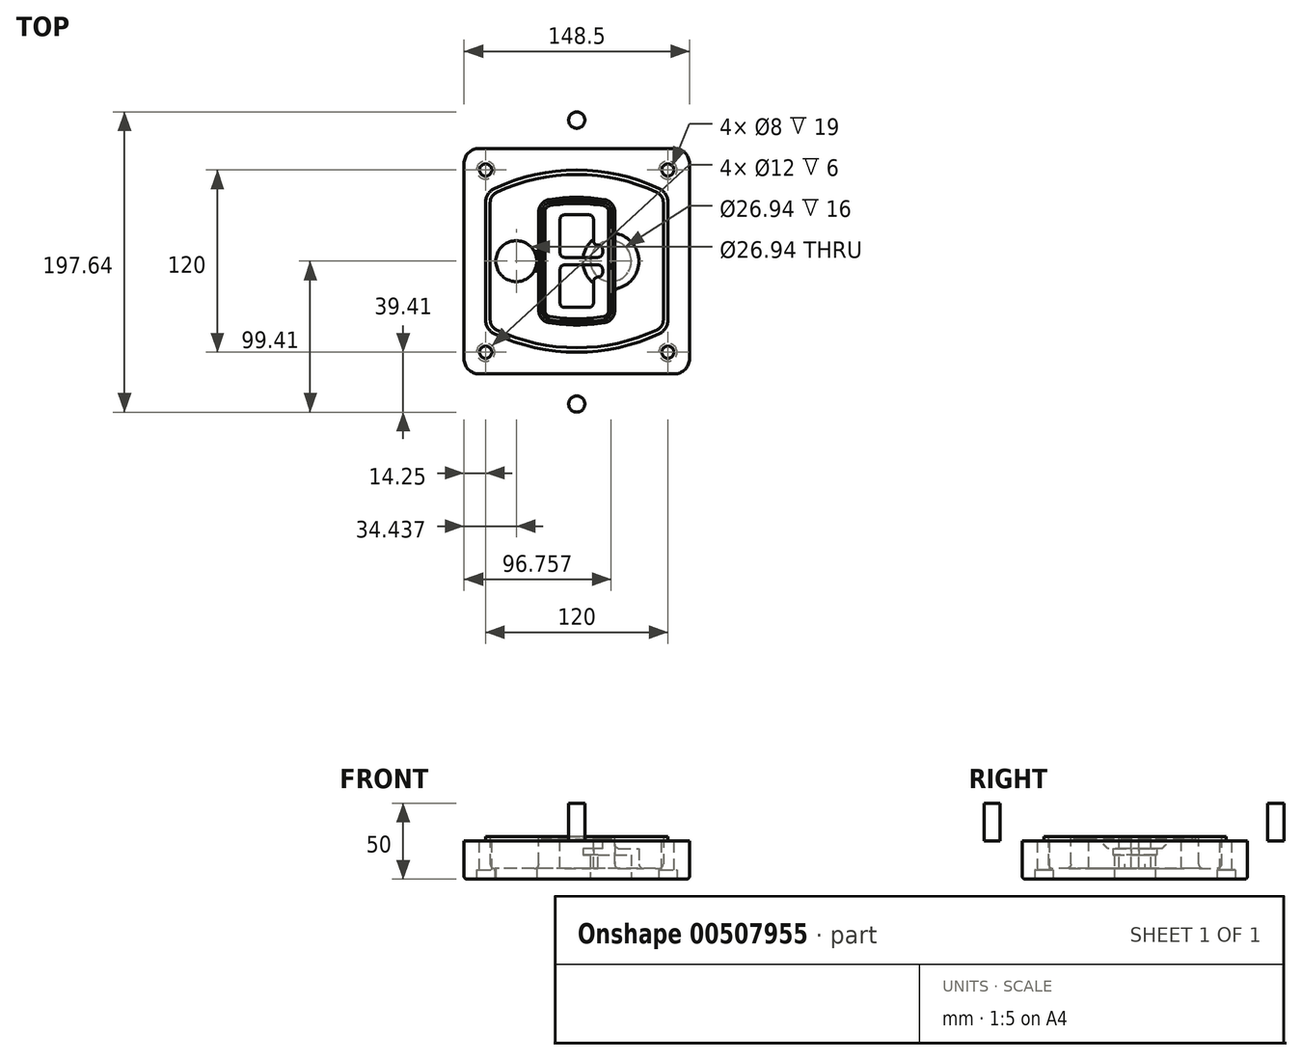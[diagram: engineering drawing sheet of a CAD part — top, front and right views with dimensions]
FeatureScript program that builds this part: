
annotation { "Feature Type Name" : "Feature", "Feature Type Description" : "" }
export const myFeature = defineFeature(function(context is Context, id is Id, definition is map)
    precondition{}
    {
        {
            var Q0;
            Q0=qCreatedBy(makeId("Top.planeOp"),FACE);
            var sketch = newSketch(context, id + "F0", { "sketchPlane" : qUnion([Q0])});
            skPoint(sketch, "E0.rect.middle", {"position": v(0, 0) * mm});
            skLineSegment(sketch, "E1.bottom", {"start": v(-64.25, -74.25) * mm, "end": v(64.25, -74.25) * mm});
            skLineSegment(sketch, "E1.top", {"start": v(-64.25, 74.25) * mm, "end": v(64.25, 74.25) * mm});
            skLineSegment(sketch, "E1.left", {"start": v(-74.25, -64.25) * mm, "end": v(-74.25, 64.25) * mm});
            skLineSegment(sketch, "E1.right", {"start": v(74.25, -64.25) * mm, "end": v(74.25, 64.25) * mm});
            skLineSegment(sketch, "E2", {"start": v(-74.25, 74.25) * mm, "end": v(74.25, -74.25) * mm, "construction": true});
            skLineSegment(sketch, "E3", {"start": v(74.25, 74.25) * mm, "end": v(-74.25, -74.25) * mm, "construction": true});
            skCircle(sketch, "E4", {"center": v(-60, 60) * mm, "radius": 4 * mm});
            skCircle(sketch, "E5", {"center": v(60, 60) * mm, "radius": 4 * mm});
            skCircle(sketch, "E6", {"center": v(60, -60) * mm, "radius": 4 * mm});
            skCircle(sketch, "E7", {"center": v(-60, -60) * mm, "radius": 4 * mm});
            skLineSegment(sketch, "E8", {"start": v(-60, 60) * mm, "end": v(60, 60) * mm, "construction": true});
            skLineSegment(sketch, "E9", {"start": v(60, 60) * mm, "end": v(60, -60) * mm, "construction": true});
            skLineSegment(sketch, "E10", {"start": v(60, -60) * mm, "end": v(-60, -60) * mm, "construction": true});
            skLineSegment(sketch, "E11", {"start": v(-60, -60) * mm, "end": v(-60, 60) * mm, "construction": true});
            skLineSegment(sketch, "E12", {"start": v(-60, 38.83) * mm, "end": v(-60, -38.83) * mm});
            skLineSegment(sketch, "E13", {"start": v(60, 38.83) * mm, "end": v(60, -38.83) * mm});
            skArc(sketch, "E14", {"start": v(54.26, 47.88) * mm, "mid": v(0, 60) * mm, "end": v(-54.26, 47.88) * mm});
            skArc(sketch, "E15", {"start": v(-54.26, -47.88) * mm, "mid": v(0, -60) * mm, "end": v(54.26, -47.88) * mm});
            skLineSegment(sketch, "E16", {"start": v(-60, 0) * mm, "end": v(60, 0) * mm, "construction": true});
            skPoint(sketch, "E17.visualSharp", {"position": v(-60, -45) * mm});
            skArc(sketch, "E17.filletArc", {"start": v(-60, -38.83) * mm, "mid": v(-58.44, -44.2) * mm, "end": v(-54.26, -47.88) * mm});
            skPoint(sketch, "E18.visualSharp", {"position": v(-60, 45) * mm});
            skArc(sketch, "E18.filletArc", {"start": v(-54.26, 47.88) * mm, "mid": v(-58.44, 44.2) * mm, "end": v(-60, 38.83) * mm});
            skPoint(sketch, "E19.visualSharp", {"position": v(60, 45) * mm});
            skArc(sketch, "E19.filletArc", {"start": v(60, 38.83) * mm, "mid": v(58.44, 44.2) * mm, "end": v(54.26, 47.88) * mm});
            skPoint(sketch, "E20.visualSharp", {"position": v(60, -45) * mm});
            skArc(sketch, "E20.filletArc", {"start": v(54.26, -47.88) * mm, "mid": v(58.44, -44.2) * mm, "end": v(60, -38.83) * mm});
            skPoint(sketch, "E21.visualSharp", {"position": v(-74.25, 74.25) * mm});
            skArc(sketch, "E21.filletArc", {"start": v(-64.25, 74.25) * mm, "mid": v(-71.32, 71.32) * mm, "end": v(-74.25, 64.25) * mm});
            skPoint(sketch, "E22.visualSharp", {"position": v(74.25, 74.25) * mm});
            skArc(sketch, "E22.filletArc", {"start": v(74.25, 64.25) * mm, "mid": v(71.32, 71.32) * mm, "end": v(64.25, 74.25) * mm});
            skPoint(sketch, "E23.visualSharp", {"position": v(74.25, -74.25) * mm});
            skArc(sketch, "E23.filletArc", {"start": v(64.25, -74.25) * mm, "mid": v(71.32, -71.32) * mm, "end": v(74.25, -64.25) * mm});
            skPoint(sketch, "E24.visualSharp", {"position": v(-74.25, -74.25) * mm});
            skArc(sketch, "E24.filletArc", {"start": v(-74.25, -64.25) * mm, "mid": v(-71.32, -71.32) * mm, "end": v(-64.25, -74.25) * mm});
            skArc(sketch, "E25.0", {"start": v(57, 38.83) * mm, "mid": v(55.9, 42.58) * mm, "end": v(52.98, 45.17) * mm});
            skLineSegment(sketch, "E25.1", {"start": v(57, 38.83) * mm, "end": v(57, -38.83) * mm});
            skArc(sketch, "E25.2", {"start": v(52.98, -45.17) * mm, "mid": v(55.9, -42.58) * mm, "end": v(57, -38.83) * mm});
            skArc(sketch, "E25.3", {"start": v(-52.98, -45.17) * mm, "mid": v(0, -57) * mm, "end": v(52.98, -45.17) * mm});
            skArc(sketch, "E25.4", {"start": v(-57, -38.83) * mm, "mid": v(-55.9, -42.58) * mm, "end": v(-52.98, -45.17) * mm});
            skArc(sketch, "E25.5", {"start": v(52.98, 45.17) * mm, "mid": v(0, 57) * mm, "end": v(-52.98, 45.17) * mm});
            skLineSegment(sketch, "E25.6", {"start": v(-57, 38.83) * mm, "end": v(-57, -38.83) * mm});
            skArc(sketch, "E25.7", {"start": v(-52.98, 45.17) * mm, "mid": v(-55.9, 42.58) * mm, "end": v(-57, 38.83) * mm});
            skArc(sketch, "E26.0", {"start": v(-55.96, 51.5) * mm, "mid": v(-61.82, 46.33) * mm, "end": v(-64, 38.83) * mm});
            skArc(sketch, "E26.1", {"start": v(55.96, 51.5) * mm, "mid": v(0, 64) * mm, "end": v(-55.96, 51.5) * mm});
            skArc(sketch, "E26.2", {"start": v(64, 38.83) * mm, "mid": v(61.82, 46.33) * mm, "end": v(55.96, 51.5) * mm});
            skLineSegment(sketch, "E26.3", {"start": v(64, 38.83) * mm, "end": v(64, -38.83) * mm});
            skArc(sketch, "E26.4", {"start": v(55.96, -51.5) * mm, "mid": v(61.82, -46.33) * mm, "end": v(64, -38.83) * mm});
            skLineSegment(sketch, "E26.5", {"start": v(-64, 38.83) * mm, "end": v(-64, -38.83) * mm});
            skArc(sketch, "E26.6", {"start": v(-55.96, -51.5) * mm, "mid": v(0, -64) * mm, "end": v(55.96, -51.5) * mm});
            skArc(sketch, "E26.7", {"start": v(-64, -38.83) * mm, "mid": v(-61.82, -46.33) * mm, "end": v(-55.96, -51.5) * mm});
            skSolve(sketch);
        }
        {
            var Q0;
            Q0=makeQuery(id+"F0.imprint","IMPRINT",FACE,{"disambiguationData":[TD([[makeQuery(id+"F0.imprint","IMPRINT",EDGE,{"derivedFrom":sQuery(id+"F0.wireOp",EDGE,"E1.bottom")}),1.0]])]});
            var Q1;
            Q1=makeQuery(id+"F0.imprint","IMPRINT",FACE,{"disambiguationData":[TD([[makeQuery(id+"F0.imprint","IMPRINT",EDGE,{"derivedFrom":sQuery(id+"F0.wireOp",EDGE,"E12")}),1.0]])]});
            var Q2;
            Q2=makeQuery(id+"F0.imprint","IMPRINT",FACE,{"disambiguationData":[TD([[makeQuery(id+"F0.imprint","IMPRINT",EDGE,{"derivedFrom":sQuery(id+"F0.wireOp",EDGE,"E25.0")}),1.0]])]});
            var Q3;
            Q3=makeQuery(id+"F0.imprint","IMPRINT",FACE,{"disambiguationData":[TD([[makeQuery(id+"F0.imprint","IMPRINT",EDGE,{"derivedFrom":sQuery(id+"F0.wireOp",EDGE,"E12")}),-1.0]])]});
            extrude(context, id + "F1", {"entities" : qUnion([Q0, Q1, Q2, Q3]), "oppositeDirection" : true, "depth" : 25 * mm});
        }
        {
            var Q0;
            Q0=makeQuery(id+"F0.imprint","IMPRINT",FACE,{"disambiguationData":[TD([[makeQuery(id+"F0.imprint","IMPRINT",EDGE,{"derivedFrom":sQuery(id+"F0.wireOp",EDGE,"E12")}),1.0]])]});
            extrude(context, id + "F2", {"entities" : qUnion([Q0]), "operationType" : NewBodyOperationType.ADD, "depth" : 3 * mm});
        }
        {
            var Q0;
            Q0=makeQuery(id+"F0.imprint","IMPRINT",FACE,{"disambiguationData":[TD([[makeQuery(id+"F0.imprint","IMPRINT",EDGE,{"derivedFrom":sQuery(id+"F0.wireOp",EDGE,"E25.0")}),1.0]])]});
            extrude(context, id + "F3", {"entities" : qUnion([Q0]), "operationType" : NewBodyOperationType.REMOVE, "oppositeDirection" : true, "depth" : 18 * mm});
        }
        {
            var Q0;
            Q0=makeQuery(id+"F2.opExtrude","CAP_FACE",FACE,{"disambiguationData":[OSD([sQuery(id+"F0.wireOp",EDGE,"E12"),sQuery(id+"F0.wireOp",EDGE,"E13"),sQuery(id+"F0.wireOp",EDGE,"E14"),sQuery(id+"F0.wireOp",EDGE,"E15"),sQuery(id+"F0.wireOp",EDGE,"E17.filletArc"),sQuery(id+"F0.wireOp",EDGE,"E18.filletArc"),sQuery(id+"F0.wireOp",EDGE,"E19.filletArc"),sQuery(id+"F0.wireOp",EDGE,"E20.filletArc"),sQuery(id+"F0.wireOp",EDGE,"E25.0"),sQuery(id+"F0.wireOp",EDGE,"E25.1"),sQuery(id+"F0.wireOp",EDGE,"E25.2"),sQuery(id+"F0.wireOp",EDGE,"E25.3"),sQuery(id+"F0.wireOp",EDGE,"E25.4"),sQuery(id+"F0.wireOp",EDGE,"E25.5"),sQuery(id+"F0.wireOp",EDGE,"E25.6"),sQuery(id+"F0.wireOp",EDGE,"E25.7")])],"isStart":false});
            var sketch = newSketch(context, id + "F4", { "sketchPlane" : qUnion([Q0])});
            skArc(sketch, "E27.0", {"start": v(-18.34, -40.45) * mm, "mid": v(0, -42) * mm, "end": v(18.34, -40.45) * mm});
            skArc(sketch, "E28.0", {"start": v(18.34, 40.45) * mm, "mid": v(0, 42) * mm, "end": v(-18.34, 40.45) * mm});
            skLineSegment(sketch, "E29", {"start": v(-25, 32.57) * mm, "end": v(-25, -32.57) * mm});
            skLineSegment(sketch, "E30", {"start": v(25, 32.57) * mm, "end": v(25, -32.57) * mm});
            skLineSegment(sketch, "E31", {"start": v(-25, 39.1) * mm, "end": v(25, 39.1) * mm, "construction": true});
            skLineSegment(sketch, "E32", {"start": v(-25, -39.1) * mm, "end": v(25, -39.1) * mm, "construction": true});
            skPoint(sketch, "E33.visualSharp", {"position": v(-25, 39.1) * mm});
            skArc(sketch, "E33.filletArc", {"start": v(-18.34, 40.45) * mm, "mid": v(-23.11, 37.73) * mm, "end": v(-25, 32.57) * mm});
            skPoint(sketch, "E34.visualSharp", {"position": v(25, 39.1) * mm});
            skArc(sketch, "E34.filletArc", {"start": v(25, 32.57) * mm, "mid": v(23.11, 37.73) * mm, "end": v(18.34, 40.45) * mm});
            skPoint(sketch, "E35.visualSharp", {"position": v(25, -39.1) * mm});
            skArc(sketch, "E35.filletArc", {"start": v(18.34, -40.45) * mm, "mid": v(23.11, -37.73) * mm, "end": v(25, -32.57) * mm});
            skPoint(sketch, "E36.visualSharp", {"position": v(-25, -39.1) * mm});
            skArc(sketch, "E36.filletArc", {"start": v(-25, -32.57) * mm, "mid": v(-23.11, -37.73) * mm, "end": v(-18.34, -40.45) * mm});
            skArc(sketch, "E37.0", {"start": v(52.98, 45.17) * mm, "mid": v(0, 57) * mm, "end": v(-52.98, 45.17) * mm});
            skArc(sketch, "E37.1", {"start": v(-52.98, 45.17) * mm, "mid": v(-55.9, 42.58) * mm, "end": v(-57, 38.83) * mm});
            skLineSegment(sketch, "E37.2", {"start": v(-57, 38.83) * mm, "end": v(-57, -38.83) * mm});
            skArc(sketch, "E37.3", {"start": v(-57, -38.83) * mm, "mid": v(-55.9, -42.58) * mm, "end": v(-52.98, -45.17) * mm});
            skArc(sketch, "E37.4", {"start": v(-52.98, -45.17) * mm, "mid": v(0, -57) * mm, "end": v(52.98, -45.17) * mm});
            skArc(sketch, "E37.5", {"start": v(52.98, -45.17) * mm, "mid": v(55.9, -42.58) * mm, "end": v(57, -38.83) * mm});
            skLineSegment(sketch, "E37.6", {"start": v(57, 38.83) * mm, "end": v(57, -38.83) * mm});
            skArc(sketch, "E37.7", {"start": v(57, 38.83) * mm, "mid": v(55.9, 42.58) * mm, "end": v(52.98, 45.17) * mm});
            skLineSegment(sketch, "E38.0", {"start": v(23, 32.57) * mm, "end": v(23, -32.57) * mm});
            skArc(sketch, "E38.1", {"start": v(18, -38.48) * mm, "mid": v(21.58, -36.44) * mm, "end": v(23, -32.57) * mm});
            skArc(sketch, "E38.2", {"start": v(-18, -38.48) * mm, "mid": v(0, -40) * mm, "end": v(18, -38.48) * mm});
            skArc(sketch, "E38.3", {"start": v(-23, -32.57) * mm, "mid": v(-21.58, -36.44) * mm, "end": v(-18, -38.48) * mm});
            skLineSegment(sketch, "E38.4", {"start": v(-23, 32.57) * mm, "end": v(-23, -32.57) * mm});
            skArc(sketch, "E38.5", {"start": v(23, 32.57) * mm, "mid": v(21.58, 36.44) * mm, "end": v(18, 38.48) * mm});
            skArc(sketch, "E38.6", {"start": v(-18, 38.48) * mm, "mid": v(-21.58, 36.44) * mm, "end": v(-23, 32.57) * mm});
            skArc(sketch, "E38.7", {"start": v(18, 38.48) * mm, "mid": v(0, 40) * mm, "end": v(-18, 38.48) * mm});
            skArc(sketch, "E39.0", {"start": v(21, 32.57) * mm, "mid": v(20.06, 35.15) * mm, "end": v(17.67, 36.5) * mm});
            skLineSegment(sketch, "E39.1", {"start": v(21, 32.57) * mm, "end": v(21, -32.57) * mm});
            skArc(sketch, "E39.2", {"start": v(17.67, -36.5) * mm, "mid": v(20.06, -35.15) * mm, "end": v(21, -32.57) * mm});
            skArc(sketch, "E39.3", {"start": v(-17.67, -36.5) * mm, "mid": v(0, -38) * mm, "end": v(17.67, -36.5) * mm});
            skArc(sketch, "E39.4", {"start": v(-21, -32.57) * mm, "mid": v(-20.06, -35.15) * mm, "end": v(-17.67, -36.5) * mm});
            skArc(sketch, "E39.5", {"start": v(17.67, 36.5) * mm, "mid": v(0, 38) * mm, "end": v(-17.67, 36.5) * mm});
            skLineSegment(sketch, "E39.6", {"start": v(-21, 32.57) * mm, "end": v(-21, -32.57) * mm});
            skArc(sketch, "E39.7", {"start": v(-17.67, 36.5) * mm, "mid": v(-20.06, 35.15) * mm, "end": v(-21, 32.57) * mm});
            skLineSegment(sketch, "E40", {"start": v(-25, 0) * mm, "end": v(25, 0) * mm, "construction": true});
            skLineSegment(sketch, "E41", {"start": v(-11, 5.5) * mm, "end": v(-11, 27.5) * mm});
            skLineSegment(sketch, "E42", {"start": v(-8, 30.5) * mm, "end": v(8, 30.5) * mm});
            skLineSegment(sketch, "E43", {"start": v(11, 27.5) * mm, "end": v(11, 13.5) * mm});
            skLineSegment(sketch, "E44", {"start": v(14, 10.5) * mm, "end": v(14, 10.5) * mm});
            skLineSegment(sketch, "E45", {"start": v(17, 7.5) * mm, "end": v(17, 5.5) * mm});
            skLineSegment(sketch, "E46", {"start": v(14, 2.5) * mm, "end": v(-8, 2.5) * mm});
            skPoint(sketch, "E47.visualSharp", {"position": v(-11, 30.5) * mm});
            skArc(sketch, "E47.filletArc", {"start": v(-8, 30.5) * mm, "mid": v(-10.12, 29.62) * mm, "end": v(-11, 27.5) * mm});
            skPoint(sketch, "E48.visualSharp", {"position": v(11, 30.5) * mm});
            skArc(sketch, "E48.filletArc", {"start": v(11, 27.5) * mm, "mid": v(10.12, 29.62) * mm, "end": v(8, 30.5) * mm});
            skPoint(sketch, "E49.visualSharp", {"position": v(11, 10.5) * mm});
            skArc(sketch, "E49.filletArc", {"start": v(11, 13.5) * mm, "mid": v(11.88, 11.38) * mm, "end": v(14, 10.5) * mm});
            skPoint(sketch, "E50.visualSharp", {"position": v(17, 10.5) * mm});
            skArc(sketch, "E50.filletArc", {"start": v(17, 7.5) * mm, "mid": v(16.12, 9.62) * mm, "end": v(14, 10.5) * mm});
            skPoint(sketch, "E51.visualSharp", {"position": v(17, 2.5) * mm});
            skArc(sketch, "E51.filletArc", {"start": v(14, 2.5) * mm, "mid": v(16.12, 3.38) * mm, "end": v(17, 5.5) * mm});
            skPoint(sketch, "E52.visualSharp", {"position": v(-11, 2.5) * mm});
            skArc(sketch, "E52.filletArc", {"start": v(-11, 5.5) * mm, "mid": v(-10.12, 3.38) * mm, "end": v(-8, 2.5) * mm});
            skLineSegment(sketch, "E53.0.MirrorCS", {"start": v(14, -2.5) * mm, "end": v(-8, -2.5) * mm});
            skArc(sketch, "E54.0.MirrorCS", {"start": v(-11, -5.5) * mm, "mid": v(-10.12, -3.38) * mm, "end": v(-8, -2.5) * mm});
            skLineSegment(sketch, "E55.0.MirrorCS", {"start": v(-11, -5.5) * mm, "end": v(-11, -27.5) * mm});
            skArc(sketch, "E56.0.MirrorCS", {"start": v(-8, -30.5) * mm, "mid": v(-10.12, -29.62) * mm, "end": v(-11, -27.5) * mm});
            skLineSegment(sketch, "E57.0.MirrorCS", {"start": v(-8, -30.5) * mm, "end": v(8, -30.5) * mm});
            skArc(sketch, "E58.0.MirrorCS", {"start": v(11, -27.5) * mm, "mid": v(10.12, -29.62) * mm, "end": v(8, -30.5) * mm});
            skLineSegment(sketch, "E59.0.MirrorCS", {"start": v(11, -27.5) * mm, "end": v(11, -13.5) * mm});
            skArc(sketch, "E60.0.MirrorCS", {"start": v(11, -13.5) * mm, "mid": v(11.88, -11.38) * mm, "end": v(14, -10.5) * mm});
            skArc(sketch, "E61.0.MirrorCS", {"start": v(17, -7.5) * mm, "mid": v(16.12, -9.62) * mm, "end": v(14, -10.5) * mm});
            skLineSegment(sketch, "E62.0.MirrorCS", {"start": v(17, -7.5) * mm, "end": v(17, -5.5) * mm});
            skArc(sketch, "E63.0.MirrorCS", {"start": v(14, -2.5) * mm, "mid": v(16.12, -3.38) * mm, "end": v(17, -5.5) * mm});
            skSolve(sketch);
        }
        {
            var Q0;
            Q0=makeQuery(id+"F4.imprint","IMPRINT",FACE,{"disambiguationData":[TD([[makeQuery(id+"F4.imprint","IMPRINT",EDGE,{"derivedFrom":sQuery(id+"F4.wireOp",EDGE,"E27.0")}),1.0]])]});
            var Q1;
            Q1=makeQuery(id+"F4.imprint","IMPRINT",FACE,{"disambiguationData":[TD([[makeQuery(id+"F4.imprint","IMPRINT",EDGE,{"derivedFrom":sQuery(id+"F4.wireOp",EDGE,"E38.0")}),-1.0]])]});
            var Q2;
            Q2=makeQuery(id+"F4.imprint","IMPRINT",FACE,{"disambiguationData":[TD([[makeQuery(id+"F4.imprint","IMPRINT",EDGE,{"derivedFrom":sQuery(id+"F4.wireOp",EDGE,"E39.0")}),1.0]])]});
            extrude(context, id + "F5", {"entities" : qUnion([Q0, Q1, Q2]), "operationType" : NewBodyOperationType.ADD, "endBound" : BoundingType.UP_TO_NEXT, "oppositeDirection" : true, "depth" : 25 * mm});
        }
        {
            var Q0;
            Q0=makeQuery(id+"F4.imprint","IMPRINT",FACE,{"disambiguationData":[TD([[makeQuery(id+"F4.imprint","IMPRINT",EDGE,{"derivedFrom":sQuery(id+"F4.wireOp",EDGE,"E38.0")}),-1.0]])]});
            extrude(context, id + "F6", {"entities" : qUnion([Q0]), "operationType" : NewBodyOperationType.REMOVE, "oppositeDirection" : true, "depth" : 2 * mm});
        }
        {
            var Q0;
            Q0=makeQuery(id+"F1.opExtrude","CAP_FACE",FACE,{"disambiguationData":[OSD([sQuery(id+"F0.wireOp",EDGE,"E1.bottom"),sQuery(id+"F0.wireOp",EDGE,"E1.top"),sQuery(id+"F0.wireOp",EDGE,"E1.left"),sQuery(id+"F0.wireOp",EDGE,"E1.right"),sQuery(id+"F0.wireOp",EDGE,"E4"),sQuery(id+"F0.wireOp",EDGE,"E5"),sQuery(id+"F0.wireOp",EDGE,"E6"),sQuery(id+"F0.wireOp",EDGE,"E7"),sQuery(id+"F0.wireOp",EDGE,"E21.filletArc"),sQuery(id+"F0.wireOp",EDGE,"E22.filletArc"),sQuery(id+"F0.wireOp",EDGE,"E23.filletArc"),sQuery(id+"F0.wireOp",EDGE,"E24.filletArc")])],"isStart":false});
            var sketch = newSketch(context, id + "F7", { "sketchPlane" : qUnion([Q0])});
            skCircle(sketch, "E64", {"center": v(22.5, 0) * mm, "radius": 13.47 * mm});
            skCircle(sketch, "E65", {"center": v(-39.81, 0) * mm, "radius": 13.47 * mm});
            skLineSegment(sketch, "E66", {"start": v(74.25, 0) * mm, "end": v(-74.25, 0) * mm});
            skCircle(sketch, "E67", {"center": v(22.5, 0) * mm, "radius": 18.47 * mm});
            skCircle(sketch, "E68", {"center": v(60, -60) * mm, "radius": 6 * mm});
            skCircle(sketch, "E69", {"center": v(-60, -60) * mm, "radius": 6 * mm});
            skCircle(sketch, "E70", {"center": v(-60, 60) * mm, "radius": 6 * mm});
            skCircle(sketch, "E71", {"center": v(60, 60) * mm, "radius": 6 * mm});
            skSolve(sketch);
        }
        {
            var Q0;
            {var subQ1=sQuery(id+"F7.wireOp",EDGE,"E66");var subQ4=sQuery(id+"F7.wireOp",EDGE,"E64");var subQ6=makeQuery(id+"F7.imprint","INTERSECT",VERTEX,{"disambiguationData":[OD(0.0)],"derivedFrom":[subQ4,subQ1]});Q0=makeQuery(id+"F7.imprint","IMPRINT",FACE,{"disambiguationData":[TD([[makeQuery(id+"F7.imprint","IMPRINT",EDGE,{"disambiguationData":[TD([[subQ6,-1.0]])],"derivedFrom":subQ4}),-1.0]])]});}
            var Q1;
            {var subQ0=sQuery(id+"F7.wireOp",EDGE,"E66");var subQ1=sQuery(id+"F7.wireOp",EDGE,"E64");var subQ3=makeQuery(id+"F7.imprint","INTERSECT",VERTEX,{"disambiguationData":[OD(0.0)],"derivedFrom":[subQ1,subQ0]});Q1=makeQuery(id+"F7.imprint","IMPRINT",FACE,{"disambiguationData":[TD([[makeQuery(id+"F7.imprint","IMPRINT",EDGE,{"disambiguationData":[TD([[subQ3,-1.0]])],"derivedFrom":subQ1}),1.0]])]});}
            var Q2;
            {var subQ0=sQuery(id+"F7.wireOp",EDGE,"E66");var subQ1=sQuery(id+"F7.wireOp",EDGE,"E64");var subQ3=makeQuery(id+"F7.imprint","INTERSECT",VERTEX,{"disambiguationData":[OD(0.0)],"derivedFrom":[subQ1,subQ0]});Q2=makeQuery(id+"F7.imprint","IMPRINT",FACE,{"disambiguationData":[TD([[makeQuery(id+"F7.imprint","IMPRINT",EDGE,{"disambiguationData":[TD([[subQ3,1.0]])],"derivedFrom":subQ1}),1.0]])]});}
            var Q3;
            {var subQ1=sQuery(id+"F7.wireOp",EDGE,"E66");var subQ4=sQuery(id+"F7.wireOp",EDGE,"E64");var subQ6=makeQuery(id+"F7.imprint","INTERSECT",VERTEX,{"disambiguationData":[OD(0.0)],"derivedFrom":[subQ4,subQ1]});Q3=makeQuery(id+"F7.imprint","IMPRINT",FACE,{"disambiguationData":[TD([[makeQuery(id+"F7.imprint","IMPRINT",EDGE,{"disambiguationData":[TD([[subQ6,1.0]])],"derivedFrom":subQ4}),-1.0]])]});}
            extrude(context, id + "F8", {"entities" : qUnion([Q0, Q1, Q2, Q3]), "operationType" : NewBodyOperationType.ADD, "oppositeDirection" : true, "depth" : 20 * mm});
        }
        {
            var Q0;
            {var subQ0=sQuery(id+"F7.wireOp",EDGE,"E66");var subQ1=sQuery(id+"F7.wireOp",EDGE,"E64");var subQ3=makeQuery(id+"F7.imprint","INTERSECT",VERTEX,{"disambiguationData":[OD(0.0)],"derivedFrom":[subQ1,subQ0]});Q0=makeQuery(id+"F7.imprint","IMPRINT",FACE,{"disambiguationData":[TD([[makeQuery(id+"F7.imprint","IMPRINT",EDGE,{"disambiguationData":[TD([[subQ3,-1.0]])],"derivedFrom":subQ1}),1.0]])]});}
            var Q1;
            {var subQ0=sQuery(id+"F7.wireOp",EDGE,"E66");var subQ1=sQuery(id+"F7.wireOp",EDGE,"E64");var subQ3=makeQuery(id+"F7.imprint","INTERSECT",VERTEX,{"disambiguationData":[OD(0.0)],"derivedFrom":[subQ1,subQ0]});Q1=makeQuery(id+"F7.imprint","IMPRINT",FACE,{"disambiguationData":[TD([[makeQuery(id+"F7.imprint","IMPRINT",EDGE,{"disambiguationData":[TD([[subQ3,1.0]])],"derivedFrom":subQ1}),1.0]])]});}
            extrude(context, id + "F9", {"entities" : qUnion([Q0, Q1]), "operationType" : NewBodyOperationType.REMOVE, "oppositeDirection" : true, "depth" : 16 * mm});
        }
        {
            var Q0;
            {var subQ0=sQuery(id+"F7.wireOp",EDGE,"E66");var subQ1=sQuery(id+"F7.wireOp",EDGE,"E65");var subQ3=makeQuery(id+"F7.imprint","INTERSECT",VERTEX,{"disambiguationData":[OD(0.0)],"derivedFrom":[subQ1,subQ0]});Q0=makeQuery(id+"F7.imprint","IMPRINT",FACE,{"disambiguationData":[TD([[makeQuery(id+"F7.imprint","IMPRINT",EDGE,{"disambiguationData":[TD([[subQ3,-1.0]])],"derivedFrom":subQ1}),1.0]])]});}
            var Q1;
            {var subQ0=sQuery(id+"F7.wireOp",EDGE,"E66");var subQ1=sQuery(id+"F7.wireOp",EDGE,"E65");var subQ3=makeQuery(id+"F7.imprint","INTERSECT",VERTEX,{"disambiguationData":[OD(0.0)],"derivedFrom":[subQ1,subQ0]});Q1=makeQuery(id+"F7.imprint","IMPRINT",FACE,{"disambiguationData":[TD([[makeQuery(id+"F7.imprint","IMPRINT",EDGE,{"disambiguationData":[TD([[subQ3,1.0]])],"derivedFrom":subQ1}),1.0]])]});}
            extrude(context, id + "F10", {"entities" : qUnion([Q0, Q1]), "operationType" : NewBodyOperationType.REMOVE, "oppositeDirection" : true, "depth" : 25 * mm});
        }
        {
            var Q0;
            Q0=makeQuery(id+"F7.imprint","IMPRINT",FACE,{"disambiguationData":[TD([[makeQuery(id+"F7.imprint","IMPRINT",EDGE,{"derivedFrom":sQuery(id+"F7.wireOp",EDGE,"E68")}),1.0]])]});
            var Q1;
            Q1=makeQuery(id+"F7.imprint","IMPRINT",FACE,{"disambiguationData":[TD([[makeQuery(id+"F7.imprint","IMPRINT",EDGE,{"derivedFrom":makeQuery(id+"F1.opExtrude","CAP_EDGE",EDGE,{"disambiguationData":[OSD([sQuery(id+"F0.wireOp",EDGE,"E5")])],"isStart":false})}),-1.0]])]});
            var Q2;
            Q2=makeQuery(id+"F7.imprint","IMPRINT",FACE,{"disambiguationData":[TD([[makeQuery(id+"F7.imprint","IMPRINT",EDGE,{"derivedFrom":sQuery(id+"F7.wireOp",EDGE,"E69")}),1.0]])]});
            var Q3;
            Q3=makeQuery(id+"F7.imprint","IMPRINT",FACE,{"disambiguationData":[TD([[makeQuery(id+"F7.imprint","IMPRINT",EDGE,{"derivedFrom":makeQuery(id+"F1.opExtrude","CAP_EDGE",EDGE,{"disambiguationData":[OSD([sQuery(id+"F0.wireOp",EDGE,"E4")])],"isStart":false})}),-1.0]])]});
            var Q4;
            Q4=makeQuery(id+"F7.imprint","IMPRINT",FACE,{"disambiguationData":[TD([[makeQuery(id+"F7.imprint","IMPRINT",EDGE,{"derivedFrom":sQuery(id+"F7.wireOp",EDGE,"E70")}),1.0]])]});
            var Q5;
            Q5=makeQuery(id+"F7.imprint","IMPRINT",FACE,{"disambiguationData":[TD([[makeQuery(id+"F7.imprint","IMPRINT",EDGE,{"derivedFrom":makeQuery(id+"F1.opExtrude","CAP_EDGE",EDGE,{"disambiguationData":[OSD([sQuery(id+"F0.wireOp",EDGE,"E7")])],"isStart":false})}),-1.0]])]});
            var Q6;
            Q6=makeQuery(id+"F7.imprint","IMPRINT",FACE,{"disambiguationData":[TD([[makeQuery(id+"F7.imprint","IMPRINT",EDGE,{"derivedFrom":sQuery(id+"F7.wireOp",EDGE,"E71")}),1.0]])]});
            var Q7;
            Q7=makeQuery(id+"F7.imprint","IMPRINT",FACE,{"disambiguationData":[TD([[makeQuery(id+"F7.imprint","IMPRINT",EDGE,{"derivedFrom":makeQuery(id+"F1.opExtrude","CAP_EDGE",EDGE,{"disambiguationData":[OSD([sQuery(id+"F0.wireOp",EDGE,"E6")])],"isStart":false})}),-1.0]])]});
            extrude(context, id + "F11", {"entities" : qUnion([Q0, Q1, Q2, Q3, Q4, Q5, Q6, Q7]), "operationType" : NewBodyOperationType.REMOVE, "oppositeDirection" : true, "depth" : 6 * mm});
        }
        {
            var Q0;
            Q0=makeQuery(id+"F9.boolean.opBoolean","COPY",FACE,{"derivedFrom":makeQuery(id+"F9.opExtrude","CAP_FACE",FACE,{"disambiguationData":[OSD([sQuery(id+"F7.wireOp",EDGE,"E64")])],"isStart":false})});
            var sketch = newSketch(context, id + "F12", { "sketchPlane" : qUnion([Q0])});
            skArc(sketch, "E72.0", {"start": v(11, 14.45) * mm, "mid": v(6.45, 9.13) * mm, "end": v(4.2, 2.5) * mm});
            skArc(sketch, "E72.1", {"start": v(4.2, -2.5) * mm, "mid": v(6.45, -9.13) * mm, "end": v(11, -14.45) * mm});
            skLineSegment(sketch, "E73", {"start": v(4.2, -2.5) * mm, "end": v(14, -2.5) * mm});
            skLineSegment(sketch, "E74.0", {"start": v(14, 2.5) * mm, "end": v(4.2, 2.5) * mm});
            skArc(sketch, "E74.1", {"start": v(14, 2.5) * mm, "mid": v(16.12, 3.38) * mm, "end": v(17, 5.5) * mm});
            skLineSegment(sketch, "E74.2", {"start": v(17, 7.5) * mm, "end": v(17, 5.5) * mm});
            skArc(sketch, "E74.3", {"start": v(17, 7.5) * mm, "mid": v(16.12, 9.62) * mm, "end": v(14, 10.5) * mm});
            skArc(sketch, "E74.4", {"start": v(11, 13.5) * mm, "mid": v(11.88, 11.38) * mm, "end": v(14, 10.5) * mm});
            skLineSegment(sketch, "E74.5", {"start": v(11, 14.45) * mm, "end": v(11, 13.5) * mm});
            skLineSegment(sketch, "E74.7", {"start": v(14, -2.5) * mm, "end": v(4.2, -2.5) * mm});
            skArc(sketch, "E74.8", {"start": v(14, -2.5) * mm, "mid": v(16.12, -3.38) * mm, "end": v(17, -5.5) * mm});
            skLineSegment(sketch, "E74.9", {"start": v(17, -7.5) * mm, "end": v(17, -5.5) * mm});
            skArc(sketch, "E74.10", {"start": v(17, -7.5) * mm, "mid": v(16.12, -9.62) * mm, "end": v(14, -10.5) * mm});
            skArc(sketch, "E74.11", {"start": v(11, -13.5) * mm, "mid": v(11.88, -11.38) * mm, "end": v(14, -10.5) * mm});
            skLineSegment(sketch, "E74.12", {"start": v(11, -14.45) * mm, "end": v(11, -13.5) * mm});
            skPoint(sketch, "E75.orphan", {"position": v(11, -27.5) * mm});
            skPoint(sketch, "E76.orphan", {"position": v(-8, -2.5) * mm});
            skPoint(sketch, "E77.orphan", {"position": v(-8, 2.5) * mm});
            skPoint(sketch, "E78.orphan", {"position": v(11, 27.5) * mm});
            skSolve(sketch);
        }
        {
            var Q0;
            {var subQ7=sQuery(id+"F12.wireOp",EDGE,"E72.0");var subQ14=sQuery(id+"F12.wireOp",EDGE,"E72.1");var subQ16=sQuery(id+"F12.wireOp",EDGE,"E74.1");var subQ18=sQuery(id+"F12.wireOp",EDGE,"E74.8");Q0=qUnion([makeQuery(id+"F12.imprint","IMPRINT",FACE,{"disambiguationData":[TD([[makeQuery(id+"F12.imprint","IMPRINT",EDGE,{"derivedFrom":subQ7}),1.0]])]}),makeQuery(id+"F12.imprint","IMPRINT",FACE,{"disambiguationData":[TD([[makeQuery(id+"F12.imprint","IMPRINT",EDGE,{"derivedFrom":subQ14}),1.0]])]}),makeQuery(id+"F12.imprint","IMPRINT",FACE,{"disambiguationData":[TD([[makeQuery(id+"F12.imprint","IMPRINT",EDGE,{"derivedFrom":subQ16}),1.0]])]}),makeQuery(id+"F12.imprint","IMPRINT",FACE,{"disambiguationData":[TD([[makeQuery(id+"F12.imprint","IMPRINT",EDGE,{"derivedFrom":subQ18}),-1.0]])]})]);}
            var Q1;
            Q1=makeQuery(id+"F5.boolean.opBoolean","SPLIT",FACE,{"disambiguationData":[TD([makeQuery(id+"F5.opExtrude","SWEPT_FACE",FACE,{"disambiguationData":[OSD([sQuery(id+"F4.wireOp",EDGE,"E41")])]})])],"derivedFrom":makeQuery(id+"F3.boolean.opBoolean","COPY",FACE,{"derivedFrom":makeQuery(id+"F3.opExtrude","CAP_FACE",FACE,{"disambiguationData":[OSD([sQuery(id+"F0.wireOp",EDGE,"E25.0"),sQuery(id+"F0.wireOp",EDGE,"E25.1"),sQuery(id+"F0.wireOp",EDGE,"E25.2"),sQuery(id+"F0.wireOp",EDGE,"E25.3"),sQuery(id+"F0.wireOp",EDGE,"E25.4"),sQuery(id+"F0.wireOp",EDGE,"E25.5"),sQuery(id+"F0.wireOp",EDGE,"E25.6"),sQuery(id+"F0.wireOp",EDGE,"E25.7")])],"isStart":false})})});
            extrude(context, id + "F13", {"entities" : qUnion([Q0]), "operationType" : NewBodyOperationType.REMOVE, "endBound" : BoundingType.UP_TO_SURFACE, "endBoundEntityFace" : qUnion([Q1]), "depth" : 25 * mm});
        }
        {
            var Q0;
            Q0=makeQuery(id+"F3.boolean.opBoolean","COPY",EDGE,{"derivedFrom":makeQuery(id+"F3.opExtrude","CAP_EDGE",EDGE,{"disambiguationData":[OSD([sQuery(id+"F0.wireOp",EDGE,"E25.6")])],"isStart":false})});
            var Q1;
            Q1=makeQuery(id+"F8.boolean.opBoolean","INTERSECT",EDGE,{"derivedFrom":[makeQuery(id+"F5.opExtrude","SWEPT_FACE",FACE,{"disambiguationData":[OSD([sQuery(id+"F4.wireOp",EDGE,"E30")])]}),makeQuery(id+"F8.opExtrude","CAP_FACE",FACE,{"disambiguationData":[OSD([sQuery(id+"F7.wireOp",EDGE,"E67")])],"isStart":false})]});
            var Q2;
            Q2=makeQuery(id+"F8.boolean.opBoolean","INTERSECT",EDGE,{"disambiguationData":[OD(1.0)],"derivedFrom":[makeQuery(id+"F5.opExtrude","SWEPT_FACE",FACE,{"disambiguationData":[OSD([sQuery(id+"F4.wireOp",EDGE,"E30")])]}),makeQuery(id+"F8.opExtrude","SWEPT_FACE",FACE,{"disambiguationData":[OSD([sQuery(id+"F7.wireOp",EDGE,"E67")])]})]});
            var Q3;
            {var subQ0=sQuery(id+"F4.wireOp",EDGE,"E30");Q3=makeQuery(id+"F8.boolean.opBoolean","SPLIT",EDGE,{"disambiguationData":[TD([makeQuery(id+"F5.opExtrude","SWEPT_FACE",FACE,{"disambiguationData":[OSD([sQuery(id+"F4.wireOp",EDGE,"E35.filletArc")])]})])],"derivedFrom":makeQuery(id+"F5.opExtrude","CAP_EDGE",EDGE,{"disambiguationData":[OSD([subQ0])],"isStart":false})});}
            var Q4;
            {var subQ0=sQuery(id+"F0.wireOp",EDGE,"E25.7");var subQ1=sQuery(id+"F0.wireOp",EDGE,"E25.1");var subQ2=sQuery(id+"F0.wireOp",EDGE,"E25.6");var subQ3=sQuery(id+"F0.wireOp",EDGE,"E25.5");var subQ4=sQuery(id+"F0.wireOp",EDGE,"E25.4");var subQ5=sQuery(id+"F0.wireOp",EDGE,"E25.0");var subQ6=sQuery(id+"F0.wireOp",EDGE,"E25.2");var subQ7=sQuery(id+"F0.wireOp",EDGE,"E25.3");Q4=makeQuery(id+"F8.boolean.opBoolean","INTERSECT",EDGE,{"derivedFrom":[makeQuery(id+"F5.boolean.opBoolean","SPLIT",FACE,{"disambiguationData":[TD([makeQuery(id+"F2.opExtrude","SWEPT_FACE",FACE,{"disambiguationData":[OSD([subQ5])]})])],"derivedFrom":makeQuery(id+"F3.boolean.opBoolean","COPY",FACE,{"derivedFrom":makeQuery(id+"F3.opExtrude","CAP_FACE",FACE,{"disambiguationData":[OSD([subQ5,subQ1,subQ6,subQ7,subQ4,subQ3,subQ2,subQ0])],"isStart":false})})}),makeQuery(id+"F8.opExtrude","SWEPT_FACE",FACE,{"disambiguationData":[OSD([sQuery(id+"F7.wireOp",EDGE,"E67")])]})]});}
            var Q5;
            Q5=makeQuery(id+"F8.boolean.opBoolean","INTERSECT",EDGE,{"disambiguationData":[OD(0.0)],"derivedFrom":[makeQuery(id+"F5.opExtrude","SWEPT_FACE",FACE,{"disambiguationData":[OSD([sQuery(id+"F4.wireOp",EDGE,"E30")])]}),makeQuery(id+"F8.opExtrude","SWEPT_FACE",FACE,{"disambiguationData":[OSD([sQuery(id+"F7.wireOp",EDGE,"E67")])]})]});
            fillet(context, id + "F14", {"entities" : qUnion([Q0, Q1, Q2, Q3, Q4, Q5]), "radius" : 3 * mm, "tangentPropagation" : true, "allowEdgeOverflow" : false});
        }
        {
            var Q0;
            Q0=makeQuery(id+"F1.opExtrude","CAP_EDGE",EDGE,{"disambiguationData":[OSD([sQuery(id+"F0.wireOp",EDGE,"E1.bottom")])],"isStart":false});
            fillet(context, id + "F15", {"entities" : qUnion([Q0]), "radius" : 2 * mm, "tangentPropagation" : true, "allowEdgeOverflow" : false});
        }
        {
            var Q0;
            Q0=qCreatedBy(makeId("Top.planeOp"),FACE);
            var sketch = newSketch(context, id + "F16", { "sketchPlane" : qUnion([Q0])});
            skLineSegment(sketch, "E79", {"start": v(0, 75.24) * mm, "end": v(0, 92.9) * mm, "construction": true});
            skCircle(sketch, "E80", {"center": v(0, 92.9) * mm, "radius": 5.33 * mm});
            skLineSegment(sketch, "E81", {"start": v(-39.75, 76.1) * mm, "end": v(-24.26, 93.03) * mm});
            skLineSegment(sketch, "E82", {"start": v(21.44, 93.03) * mm, "end": v(38.73, 75.24) * mm});
            skLineSegment(sketch, "E83.MirrorCS", {"start": v(21.44, -241.53) * mm, "end": v(38.73, -223.74) * mm});
            skArc(sketch, "E84", {"start": v(21.44, 93.03) * mm, "mid": v(-1.4, 116.78) * mm, "end": v(-24.26, 93.03) * mm});
            skLineSegment(sketch, "E85", {"start": v(-39.75, -75.3) * mm, "end": v(-24.26, -94.07) * mm});
            skLineSegment(sketch, "E86", {"start": v(38.73, -75.3) * mm, "end": v(26.26, -94.07) * mm});
            skLineSegment(sketch, "E87", {"start": v(0, -74.16) * mm, "end": v(0, -94.07) * mm, "construction": true});
            skCircle(sketch, "E88", {"center": v(0, -94.07) * mm, "radius": 5.33 * mm});
            skArc(sketch, "E89", {"start": v(-24.26, -94.07) * mm, "mid": v(1, -124.08) * mm, "end": v(26.26, -94.07) * mm});
            skSolve(sketch);
        }
        {
            var Q0;
            Q0 = qSketchRegion(id + "F16", true);
            extrude(context, id + "F17", {"entities" : qUnion([Q0]), "depth" : 25 * mm});
        }
    });
